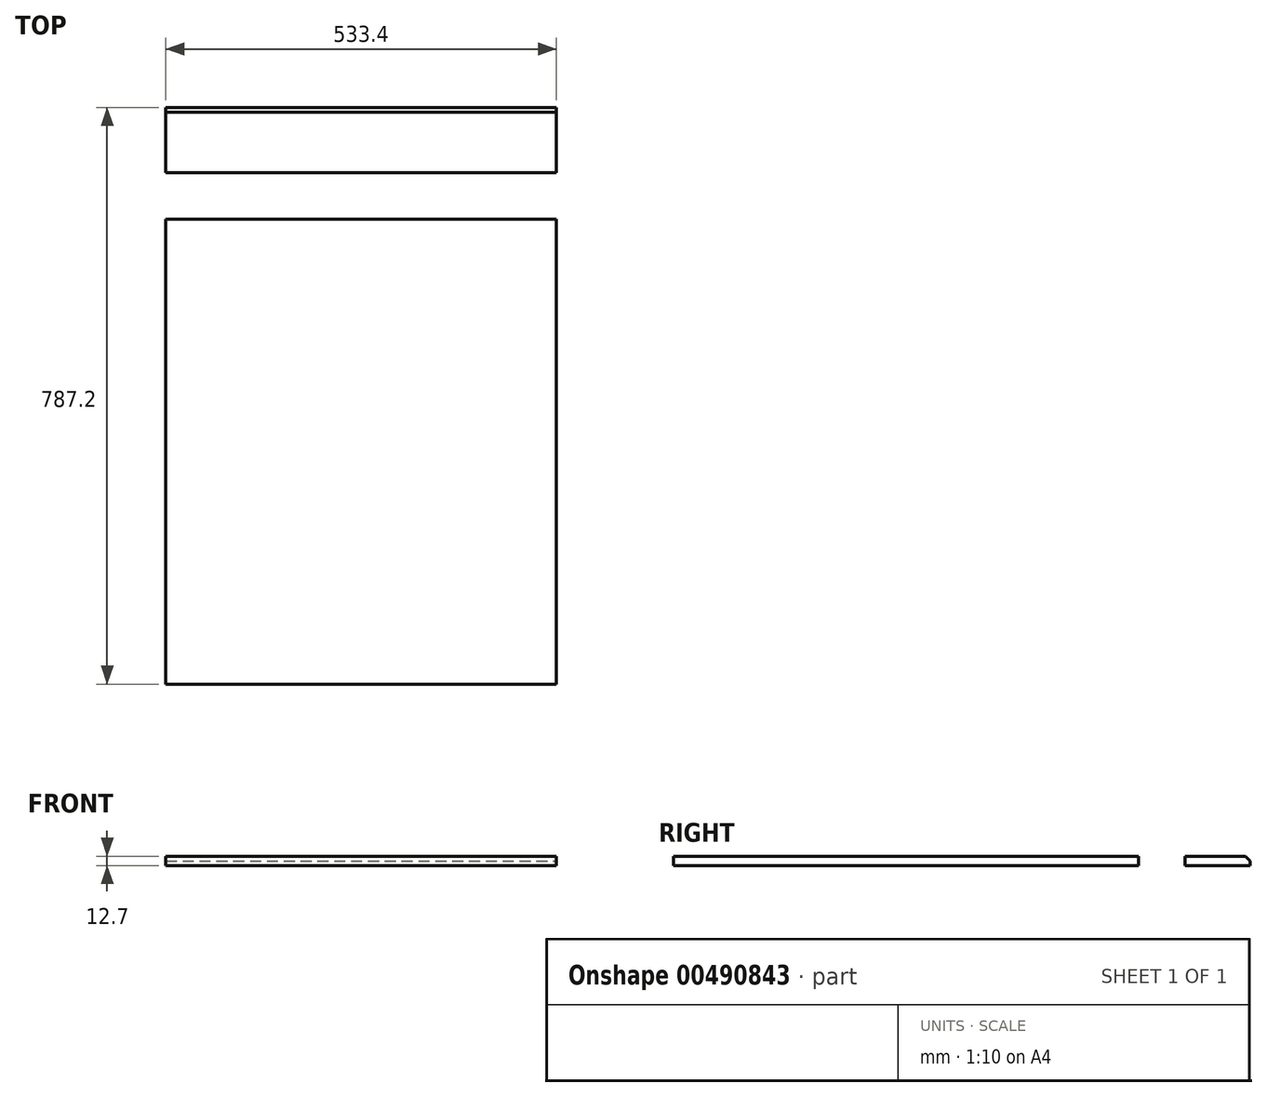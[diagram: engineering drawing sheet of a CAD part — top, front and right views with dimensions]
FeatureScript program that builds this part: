
annotation { "Feature Type Name" : "Feature", "Feature Type Description" : "" }
export const myFeature = defineFeature(function(context is Context, id is Id, definition is map)
    precondition{}
    {
        {
            var Q0;
            Q0=qCreatedBy(makeId("Top.planeOp"),FACE);
            var sketch = newSketch(context, id + "F0", { "sketchPlane" : qUnion([Q0])});
            skLineSegment(sketch, "E0.bottom", {"start": v(0, 0) * mm, "end": v(533.4, 0) * mm});
            skLineSegment(sketch, "E0.top", {"start": v(0, 635) * mm, "end": v(533.4, 635) * mm});
            skLineSegment(sketch, "E0.left", {"start": v(0, 0) * mm, "end": v(0, 635) * mm});
            skLineSegment(sketch, "E0.right", {"start": v(533.4, 0) * mm, "end": v(533.4, 635) * mm});
            skLineSegment(sketch, "E1.bottom", {"start": v(0, 698.3) * mm, "end": v(533.4, 698.3) * mm});
            skLineSegment(sketch, "E1.top", {"start": v(0, 787.2) * mm, "end": v(533.4, 787.2) * mm});
            skLineSegment(sketch, "E1.left", {"start": v(0, 698.3) * mm, "end": v(0, 787.2) * mm});
            skLineSegment(sketch, "E1.right", {"start": v(533.4, 698.3) * mm, "end": v(533.4, 787.2) * mm});
            skSolve(sketch);
        }
        {
            var Q0;
            Q0=makeQuery(id+"F0.imprint","IMPRINT",FACE,{"disambiguationData":[TD([[makeQuery(id+"F0.imprint","IMPRINT",EDGE,{"derivedFrom":sQuery(id+"F0.wireOp",EDGE,"E1.bottom")}),1.0]])]});
            var Q1;
            Q1=makeQuery(id+"F0.imprint","IMPRINT",FACE,{"disambiguationData":[TD([[makeQuery(id+"F0.imprint","IMPRINT",EDGE,{"derivedFrom":sQuery(id+"F0.wireOp",EDGE,"E0.bottom")}),1.0]])]});
            extrude(context, id + "F1", {"entities" : qUnion([Q0, Q1]), "depth" : 12.7 * mm, "offsetDistance" : 25.4 * mm});
        }
        {
            var Q0;
            Q0=makeQuery(id+"F1.opExtrude","CAP_EDGE",EDGE,{"disambiguationData":[OSD([sQuery(id+"F0.wireOp",EDGE,"E1.top")])],"isStart":false});
            chamfer(context, id + "F2", {"entities" : qUnion([Q0]), "width" : 6.35 * mm, "tangentPropagation" : true});
        }
        {
            var Q0;
            Q0=makeQuery(id+"F1.opExtrude","SWEPT_BODY",BODY,{"disambiguationData":[OSD([sQuery(id+"F0.wireOp",EDGE,"E0.bottom"),sQuery(id+"F0.wireOp",EDGE,"E0.top"),sQuery(id+"F0.wireOp",EDGE,"E0.left"),sQuery(id+"F0.wireOp",EDGE,"E0.right")])]});
            var Q1;
            Q1=makeQuery(id+"F1.opExtrude","SWEPT_BODY",BODY,{"disambiguationData":[OSD([sQuery(id+"F0.wireOp",EDGE,"E1.bottom"),sQuery(id+"F0.wireOp",EDGE,"E1.top"),sQuery(id+"F0.wireOp",EDGE,"E1.left"),sQuery(id+"F0.wireOp",EDGE,"E1.right")])]});
            transform(context, id + "F3", {"entities" : qUnion([Q0, Q1]), "transformType" : TransformType.TRANSLATION_3D, "dx" : -1016 * mm, "dy" : 0 * mm, "dz" : 0 * mm, "makeCopy" : false});
        }
    });
